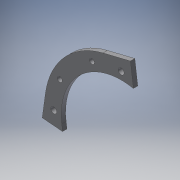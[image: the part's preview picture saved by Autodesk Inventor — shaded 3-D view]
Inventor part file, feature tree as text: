
AUTODESK INVENTOR PART (.ipt)
format: ipt  version: 2019.3 (Build 233278000, 278)  size: 115,712 bytes
history: native  units: mm
features: other x4, reference x3, extrude x1, sketch x1
ambient origin geometry x8: Origin, YZ Plane, XZ Plane, XY Plane, X Axis, Y Axis, Z Axis, Center Point
bodies: Solid1 (feature_tree)
feature tree (9):
  extrude  "Extrusion1"  Depth=4.4mm
  sketch  "Sketch1"  dims[d2=25.0mm d3=5.0mm d4=5.0mm d6=10.0mm d7=4.4mm d8=0.0mm]
  reference  "Reference6"
  reference  "Reference7"
  reference  "Reference8"
  other  "<userpath>\Desktop\3dprojects\OpenEmoto\Swingarm3\Swingarm3.iam"
  other  "Swingarm3.iam"
  other  "Denzel4500Motor:1"
  other  "Swingarm3:1"
